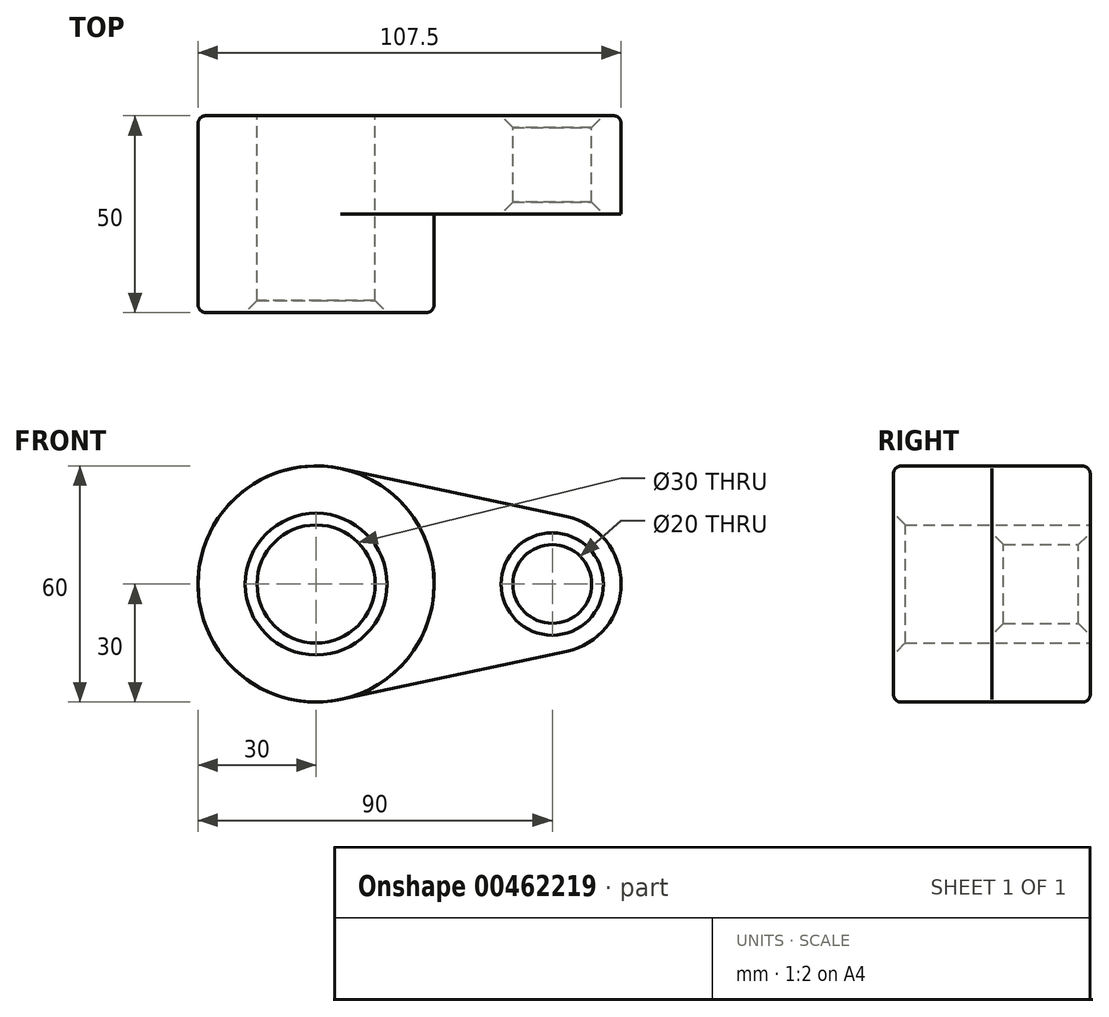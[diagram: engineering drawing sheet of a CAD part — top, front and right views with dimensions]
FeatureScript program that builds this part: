
annotation { "Feature Type Name" : "Feature", "Feature Type Description" : "" }
export const myFeature = defineFeature(function(context is Context, id is Id, definition is map)
    precondition{}
    {
        {
            var Q0;
            Q0=qCreatedBy(makeId("Front.planeOp"),FACE);
            var sketch = newSketch(context, id + "F0", { "sketchPlane" : qUnion([Q0])});
            skCircle(sketch, "E0", {"center": v(0, 0) * mm, "radius": 30 * mm});
            skCircle(sketch, "E1", {"center": v(60, 0) * mm, "radius": 17.5 * mm});
            skCircle(sketch, "E2", {"center": v(0, 0) * mm, "radius": 15 * mm});
            skCircle(sketch, "E3", {"center": v(60, 0) * mm, "radius": 10 * mm});
            skLineSegment(sketch, "E4", {"start": v(6.25, 29.34) * mm, "end": v(63.65, 17.12) * mm});
            skLineSegment(sketch, "E5.MirrorCS", {"start": v(6.25, -29.34) * mm, "end": v(63.65, -17.12) * mm});
            skSolve(sketch);
        }
        {
            var Q0;
            Q0 = qSketchRegion(id + "F0", true);
            extrude(context, id + "F1", {"entities" : qUnion([Q0]), "depth" : 25 * mm});
        }
        {
            var Q0;
            Q0=makeQuery(id+"F0.imprint","IMPRINT",FACE,{"disambiguationData":[TD([[makeQuery(id+"F0.imprint","IMPRINT",EDGE,{"derivedFrom":sQuery(id+"F0.wireOp",EDGE,"E2")}),-1.0]])]});
            extrude(context, id + "F2", {"entities" : qUnion([Q0]), "operationType" : NewBodyOperationType.ADD, "depth" : 50 * mm});
        }
        {
            var Q0;
            Q0=makeQuery(id+"F2.opExtrude","CAP_EDGE",EDGE,{"disambiguationData":[OSD([sQuery(id+"F0.wireOp",EDGE,"E0")])],"isStart":false});
            var Q1;
            Q1=makeQuery(id+"F1.opExtrude","CAP_EDGE",EDGE,{"disambiguationData":[OSD([sQuery(id+"F0.wireOp",EDGE,"RExzMfOa-nDnj-wNRi-mYEG-QKASRI7ZvtUk")])],"isStart":true});
            var Q2;
            Q2=makeQuery(id+"F1.opExtrude","CAP_EDGE",EDGE,{"disambiguationData":[OSD([sQuery(id+"F0.wireOp",EDGE,"E5.MirrorCS")])],"isStart":true});
            fillet(context, id + "F3", {"entities" : qUnion([Q0, Q1, Q2]), "radius" : 2 * mm, "tangentPropagation" : true, "allowEdgeOverflow" : false});
        }
        {
            var Q0;
            Q0=makeQuery(id+"F2.opExtrude","CAP_EDGE",EDGE,{"disambiguationData":[OSD([sQuery(id+"F0.wireOp",EDGE,"E2")])],"isStart":false});
            var Q1;
            Q1=makeQuery(id+"F1.opExtrude","SWEPT_FACE",FACE,{"disambiguationData":[OSD([sQuery(id+"F0.wireOp",EDGE,"E3")])]});
            chamfer(context, id + "F4", {"entities" : qUnion([Q0, Q1]), "width" : 3 * mm, "tangentPropagation" : true});
        }
    });
